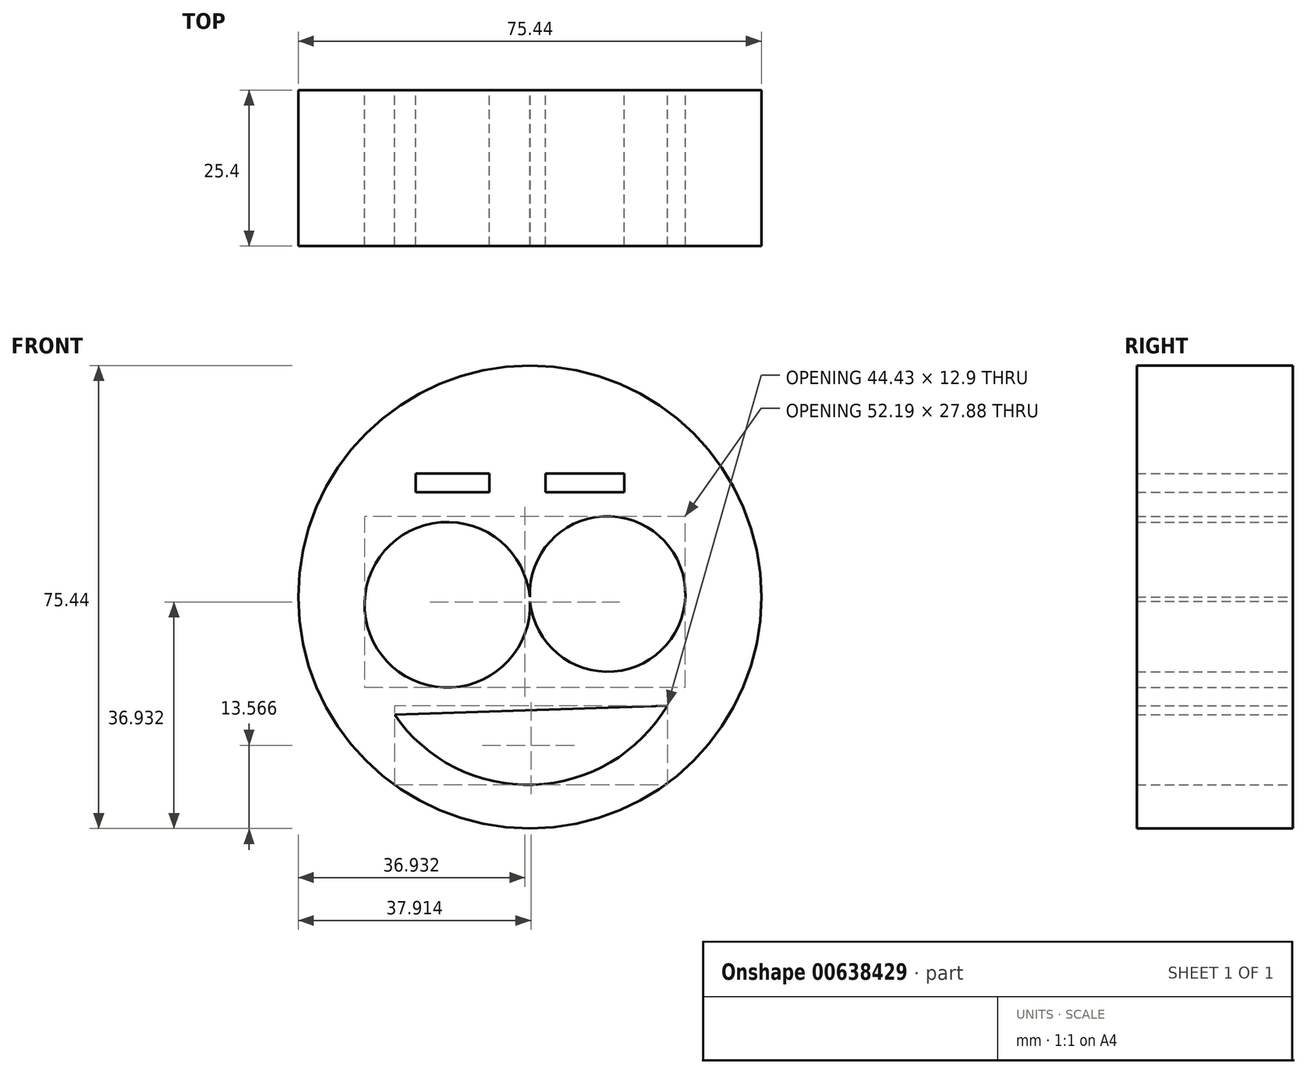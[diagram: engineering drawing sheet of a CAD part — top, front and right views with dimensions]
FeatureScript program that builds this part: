
annotation { "Feature Type Name" : "Feature", "Feature Type Description" : "" }
export const myFeature = defineFeature(function(context is Context, id is Id, definition is map)
    precondition{}
    {
        {
            var Q0;
            Q0=qCreatedBy(makeId("Front.planeOp"),FACE);
            var sketch = newSketch(context, id + "F0", { "sketchPlane" : qUnion([Q0])});
            skCircle(sketch, "E0", {"center": v(24.85, 26.42) * mm, "radius": 37.72 * mm});
            skPoint(sketch, "E0.first.point", {"position": v(0, -1.96) * mm});
            skPoint(sketch, "E0.second.point", {"position": v(46.64, 57.2) * mm});
            skPoint(sketch, "E0.third.point", {"position": v(-6.93, 46.73) * mm});
            skCircle(sketch, "E1", {"center": v(37.51, 26.92) * mm, "radius": 12.67 * mm});
            skPoint(sketch, "E1.second.point", {"position": v(48.22, 33.7) * mm});
            skPoint(sketch, "E1.third.point", {"position": v(26.26, 21.1) * mm});
            skCircle(sketch, "E2", {"center": v(11.42, 25.16) * mm, "radius": 13.49 * mm});
            skPoint(sketch, "E2.second.point", {"position": v(-2, 26.42) * mm});
            skPoint(sketch, "E2.third.point", {"position": v(5.82, 12.89) * mm});
            skLineSegment(sketch, "E3", {"start": v(10.44, 0) * mm, "end": v(42.33, 6.63) * mm});
            skLineSegment(sketch, "E4", {"start": v(28.01, 13.7) * mm, "end": v(21.14, 8.15) * mm});
            skLineSegment(sketch, "E5", {"start": v(21.14, 8.15) * mm, "end": v(34.7, 10.06) * mm});
            skLineSegment(sketch, "E6", {"start": v(6.24, 46.53) * mm, "end": v(18.27, 46.53) * mm});
            skLineSegment(sketch, "E7", {"start": v(27.44, 46.53) * mm, "end": v(40.23, 46.53) * mm});
            skLineSegment(sketch, "E8", {"start": v(6.24, 46.53) * mm, "end": v(6.24, 43.48) * mm});
            skLineSegment(sketch, "E9", {"start": v(6.24, 43.48) * mm, "end": v(18.27, 43.48) * mm});
            skLineSegment(sketch, "E10", {"start": v(18.27, 46.53) * mm, "end": v(18.27, 43.48) * mm});
            skLineSegment(sketch, "E11", {"start": v(40.23, 46.53) * mm, "end": v(40.23, 43.48) * mm});
            skLineSegment(sketch, "E12", {"start": v(40.23, 43.48) * mm, "end": v(27.44, 43.48) * mm});
            skLineSegment(sketch, "E13", {"start": v(27.44, 43.48) * mm, "end": v(27.44, 46.53) * mm});
            skSolve(sketch);
        }
        {
            var Q0;
            Q0=makeQuery(id+"F0.imprint","IMPRINT",FACE,{"disambiguationData":[TD([[makeQuery(id+"F0.imprint","IMPRINT",EDGE,{"derivedFrom":sQuery(id+"F0.wireOp",EDGE,"E0")}),1.0]])]});
            var sketch = newSketch(context, id + "F1", { "sketchPlane" : qUnion([Q0])});
            skLineSegment(sketch, "E14", {"start": v(16.36, -9.6) * mm, "end": v(25.34, -23.35) * mm});
            skLineSegment(sketch, "E15", {"start": v(25.34, -23.35) * mm, "end": v(30.88, -11.13) * mm});
            skLineSegment(sketch, "E16", {"start": v(20.1, -15.34) * mm, "end": v(16.36, -9.6) * mm});
            skSolve(sketch);
        }
        {
            var Q0;
            Q0 = qSketchRegion(id + "F0", true);
            extrude(context, id + "F2", {"entities" : qUnion([Q0]), "depth" : 25.4 * mm, "offsetDistance" : 25.4 * mm});
        }
        {
            var Q0;
            Q0=makeQuery(id+"F1.imprint","IMPRINT",FACE,{"disambiguationData":[TD([[makeQuery(id+"F1.imprint","IMPRINT",EDGE,{"derivedFrom":makeQuery(id+"F0.imprint","IMPRINT",EDGE,{"derivedFrom":sQuery(id+"F0.wireOp",EDGE,"E0")})}),1.0]])]});
            var sketch = newSketch(context, id + "F3", { "sketchPlane" : qUnion([Q0])});
            skArc(sketch, "E17", {"start": v(2.83, 7.22) * mm, "mid": v(25.45, -4.18) * mm, "end": v(47.26, 8.72) * mm});
            skLineSegment(sketch, "E18", {"start": v(47.26, 8.72) * mm, "end": v(2.83, 7.22) * mm});
            skSolve(sketch);
        }
        {
            var Q0;
            Q0=makeQuery(id+"F3.imprint","IMPRINT",FACE,{"disambiguationData":[TD([[makeQuery(id+"F3.imprint","IMPRINT",EDGE,{"derivedFrom":sQuery(id+"F3.wireOp",EDGE,"E17")}),1.0]])]});
            extrude(context, id + "F4", {"entities" : qUnion([Q0]), "operationType" : NewBodyOperationType.REMOVE, "depth" : 230.89 * mm, "offsetDistance" : 25.4 * mm});
        }
    });
